# Revit family: Double Fixed
name_source: partatom
category: Windows
units: mm (PartAtom-declared; Revit-internal decimal feet)

## family parameters
Always vertical = Yes
Cut with Voids When Loaded = Yes
Host = Wall
OmniClass Number = 23.30.20.00
OmniClass Title = Windows
Room Calculation Point = No
Shared = No

## types (8) — shared parameters
Analytic Construction = <None>
Brick Head Material = <By Category>
Brick Sill Material = <By Category>
Brick Sill Projection = 0' - 5"
Brick head Offset = 8' - 0"
Ext Wall To Ext FC Panel Trim = 0' - 1"
Ext Wall to Int Of Brick Sill = 0' - 0"
FC Trim Panel = No
FC Trim material = <By Category>
Frame Material = <By Category>
Frame Width = 0' - 1"
Glass Material = <By Category>
Glass Width = 0' - 0 1/4"
Grille Material = Default Window Frame
No Sill Visibility = Yes
Pane Width = 0' - 0 1/2"
Precast Sill = No
Precast Sill Beginning of Slant to Ext of Wall = 0' - 0"
Precast Sill Material = <By Category>
Precast Sill Profile Height = 0' - 2 3/4"
Precast Sill Profile Inset Into Wall = 0' - 4"
Precast Sill Profile Slant Length = 0' - 3"
Sash Material = <By Category>
Sash Width = 0' - 1 1/2"
Sill Depth = 0' - 2"
Sill Visibility = No
Tag Type = FX
Wall Closure = By host
zero-valued in all types: Tag Height Inches, Tag Width Inches

## per-type parameters (varying)
| type | Brick Header | Brick Sill | Default Sill Height | Description | Double Window | Ext Wall To Ext Brick Head | Grille Panel Height | Grille Panel Width | Height | Tag Height Feet | Tag Width Feet | Width |
| 3030 FX | No | No | 5' - 0" |  | No | 0' - 1" | 2' - 7" | 2' - 7" | 3' - 0" | 3 | 3 | 3' - 0" |
| 3060 FX | No | No | 2' - 0" |  | No | 0' - 1" | 5' - 7" | 2' - 7" | 6' - 0" | 6 | 3 | 3' - 0" |
| 6060 FX Double | No | No | 2' - 0" |  | Yes | 0' - 1" | 5' - 7" | 5' - 7" | 6' - 0" | 6 | 6 | 6' - 0" |
| 6030 FX Double | No | No | 5' - 0" |  | Yes | 0' - 1" | 2' - 7" | 5' - 7" | 3' - 0" | 3 | 6 | 6' - 0" |
| 3030 FX Double | No | No | 5' - 0" |  | Yes | 0' - 1" | 2' - 7" | 2' - 7" | 3' - 0" | 3 | 3 | 3' - 0" |
| 6060 FX Double Brick Grill | Yes | Yes | 2' - 0" | FIXED | Yes | 0' - 5" | 5' - 7" | 5' - 7" | 6' - 0" | 6 | 6 | 6' - 0" |
| 6030 FX Double Brick | Yes | Yes | 5' - 0" | FIXED | Yes | 0' - 5" | 2' - 7" | 5' - 7" | 3' - 0" | 3 | 6 | 6' - 0" |
| 6060 FX Double Brick | Yes | Yes | 2' - 0" |  | Yes | 0' - 5" | 5' - 7" | 5' - 7" | 6' - 0" | 6 | 6 | 6' - 0" |

## geometry (parser evidence)
native form markers: Sweep x95
no freeform markers — native parametric forms only
